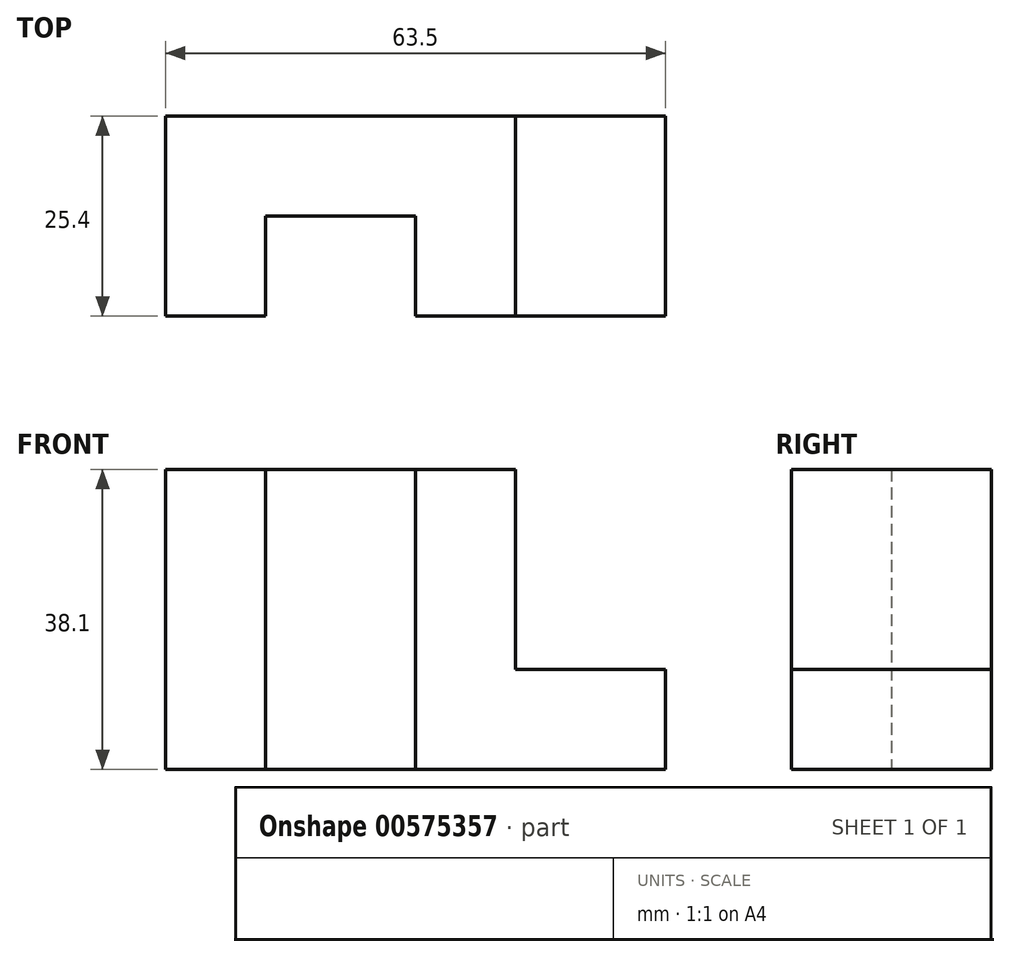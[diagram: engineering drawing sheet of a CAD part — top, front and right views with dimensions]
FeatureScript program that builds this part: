
annotation { "Feature Type Name" : "Feature", "Feature Type Description" : "" }
export const myFeature = defineFeature(function(context is Context, id is Id, definition is map)
    precondition{}
    {
        {
            var Q0;
            Q0=qCreatedBy(makeId("Top.planeOp"),FACE);
            var sketch = newSketch(context, id + "F0", { "sketchPlane" : qUnion([Q0])});
            skLineSegment(sketch, "E0", {"start": v(0, 0) * mm, "end": v(0, 25.4) * mm});
            skLineSegment(sketch, "E1", {"start": v(0, 25.4) * mm, "end": v(63.5, 25.4) * mm});
            skLineSegment(sketch, "E2", {"start": v(63.5, 25.4) * mm, "end": v(63.5, 0) * mm});
            skLineSegment(sketch, "E3", {"start": v(63.5, 0) * mm, "end": v(44.45, 0) * mm});
            skLineSegment(sketch, "E4", {"start": v(12.7, 0) * mm, "end": v(12.7, 12.7) * mm});
            skLineSegment(sketch, "E5", {"start": v(12.7, 12.7) * mm, "end": v(31.75, 12.7) * mm});
            skLineSegment(sketch, "E6", {"start": v(31.75, 12.7) * mm, "end": v(31.75, 0) * mm});
            skLineSegment(sketch, "E7", {"start": v(12.7, 0) * mm, "end": v(0, 0) * mm});
            skLineSegment(sketch, "E8", {"start": v(12.7, 0) * mm, "end": v(12.7, 0) * mm});
            skLineSegment(sketch, "E9", {"start": v(44.45, 25.4) * mm, "end": v(44.45, 0) * mm});
            skLineSegment(sketch, "E10", {"start": v(44.45, 0) * mm, "end": v(31.75, 0) * mm});
            skSolve(sketch);
        }
        {
            var Q0;
            {var subQ1=sQuery(id+"F0.wireOp",EDGE,"E0");Q0=makeQuery(id+"F0.imprint","IMPRINT",FACE,{"disambiguationData":[TD([[makeQuery(id+"F0.imprint","IMPRINT",EDGE,{"derivedFrom":subQ1}),-1.0]])]});}
            extrude(context, id + "F1", {"entities" : qUnion([Q0]), "depth" : 38.1 * mm, "offsetDistance" : 25.4 * mm});
        }
        {
            var Q0;
            Q0 = qSketchRegion(id + "F0", true);
            extrude(context, id + "F2", {"entities" : qUnion([Q0]), "operationType" : NewBodyOperationType.ADD, "depth" : 12.7 * mm, "offsetDistance" : 25.4 * mm});
        }
    });
